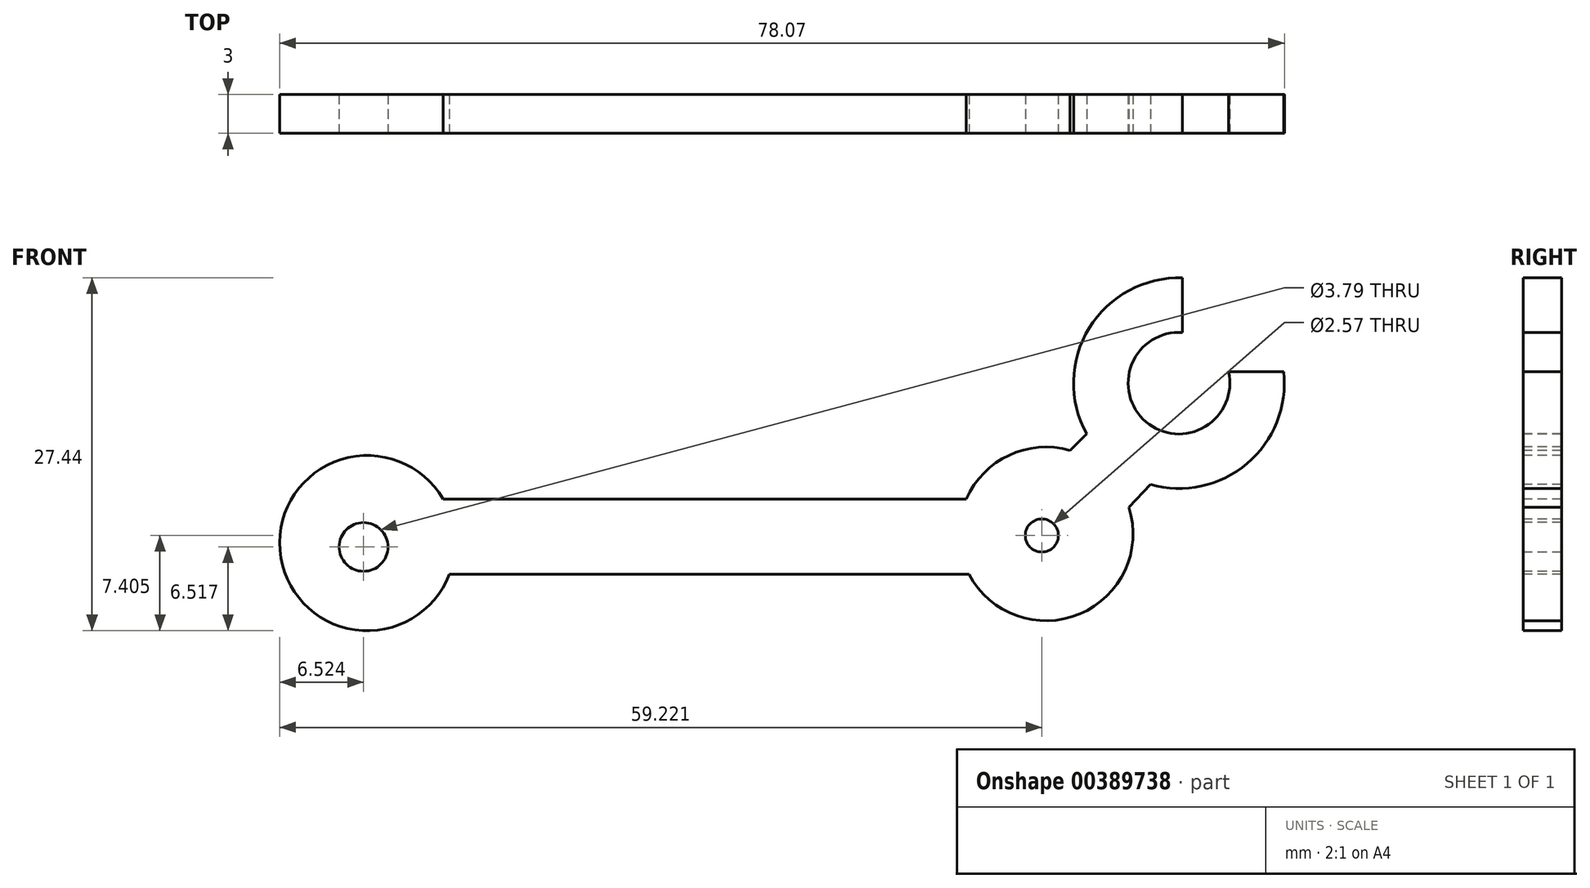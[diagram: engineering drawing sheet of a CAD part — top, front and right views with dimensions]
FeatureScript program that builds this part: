
annotation { "Feature Type Name" : "Feature", "Feature Type Description" : "" }
export const myFeature = defineFeature(function(context is Context, id is Id, definition is map)
    precondition{}
    {
        {
            var Q0;
            Q0=qCreatedBy(makeId("Front.planeOp"),FACE);
            var sketch = newSketch(context, id + "F0", { "sketchPlane" : qUnion([Q0])});
            skPoint(sketch, "E0.visualSharp", {"position": v(0, 0) * mm});
            skCircle(sketch, "E1", {"center": v(-5, 5.75) * mm, "radius": 6.76 * mm});
            skCircle(sketch, "E2", {"center": v(-57.73, 5.03) * mm, "radius": 6.82 * mm});
            skLineSegment(sketch, "E3", {"start": v(-51.84, 8.46) * mm, "end": v(-11.19, 8.46) * mm});
            skLineSegment(sketch, "E4", {"start": v(-51.36, 2.6) * mm, "end": v(-10.98, 2.6) * mm});
            skCircle(sketch, "E5", {"center": v(5.33, 17.47) * mm, "radius": 8.19 * mm});
            skLineSegment(sketch, "E6", {"start": v(1.43, 7.81) * mm, "end": v(3.1, 9.59) * mm});
            skLineSegment(sketch, "E7", {"start": v(-3.14, 12.24) * mm, "end": v(-1.85, 13.52) * mm});
            skLineSegment(sketch, "E8", {"start": v(9.18, 18.36) * mm, "end": v(13.47, 18.36) * mm});
            skCircle(sketch, "E9", {"center": v(5.33, 17.47) * mm, "radius": 3.95 * mm});
            skLineSegment(sketch, "E10", {"start": v(5.6, 21.4) * mm, "end": v(5.6, 25.65) * mm});
            skPoint(sketch, "E11", {"position": v(6.42, 21.26) * mm});
            skPoint(sketch, "E12", {"position": v(9.01, 18.9) * mm});
            skPoint(sketch, "E13", {"position": v(13.4, 18.9) * mm});
            skPoint(sketch, "E14", {"position": v(6.18, 25.61) * mm});
            skPoint(sketch, "E15", {"position": v(11.79, 22.5) * mm});
            skPoint(sketch, "E16", {"position": v(5.6, 21.4) * mm});
            skPoint(sketch, "E17", {"position": v(9.18, 18.36) * mm});
            skPoint(sketch, "E18", {"position": v(8.48, 19.85) * mm});
            skSolve(sketch);
        }
        {
            var Q0;
            {var subQ0=sQuery(id+"F0.wireOp",EDGE,"E2");var subQ1=makeQuery(id+"F0.imprint","INTERSECT",VERTEX,{"derivedFrom":[subQ0,sQuery(id+"F0.wireOp",EDGE,"E3")]});Q0=makeQuery(id+"F0.imprint","IMPRINT",FACE,{"disambiguationData":[TD([[makeQuery(id+"F0.imprint","IMPRINT",EDGE,{"disambiguationData":[TD([[subQ1,-1.0]])],"derivedFrom":subQ0}),1.0]])]});}
            var Q1;
            {var subQ0=sQuery(id+"F0.wireOp",EDGE,"E1");var subQ1=makeQuery(id+"F0.imprint","INTERSECT",VERTEX,{"derivedFrom":[subQ0,sQuery(id+"F0.wireOp",EDGE,"E6")]});Q1=makeQuery(id+"F0.imprint","IMPRINT",FACE,{"disambiguationData":[TD([[makeQuery(id+"F0.imprint","IMPRINT",EDGE,{"disambiguationData":[TD([[subQ1,-1.0]])],"derivedFrom":subQ0}),1.0]])]});}
            var Q2;
            {var subQ0=sQuery(id+"F0.wireOp",EDGE,"E3");Q2=makeQuery(id+"F0.imprint","IMPRINT",FACE,{"disambiguationData":[TD([[makeQuery(id+"F0.imprint","IMPRINT",EDGE,{"derivedFrom":subQ0}),-1.0]])]});}
            var Q3;
            {var subQ0=sQuery(id+"F0.wireOp",EDGE,"E6");Q3=makeQuery(id+"F0.imprint","IMPRINT",FACE,{"disambiguationData":[TD([[makeQuery(id+"F0.imprint","IMPRINT",EDGE,{"derivedFrom":subQ0}),1.0]])]});}
            var Q4;
            {var subQ2=sQuery(id+"F0.wireOp",EDGE,"E8");Q4=makeQuery(id+"F0.imprint","IMPRINT",FACE,{"disambiguationData":[TD([[makeQuery(id+"F0.imprint","IMPRINT",EDGE,{"derivedFrom":subQ2}),-1.0]])]});}
            extrude(context, id + "F1", {"entities" : qUnion([Q0, Q1, Q2, Q3, Q4]), "oppositeDirection" : true, "depth" : 3 * mm});
        }
        {
            var Q0;
            Q0=qCreatedBy(makeId("Front.planeOp"),FACE);
            var sketch = newSketch(context, id + "F2", { "sketchPlane" : qUnion([Q0])});
            skCircle(sketch, "E19", {"center": v(-5.33, 5.63) * mm, "radius": 1.28 * mm});
            skCircle(sketch, "E20", {"center": v(-58.03, 4.74) * mm, "radius": 1.9 * mm});
            skSolve(sketch);
        }
        {
            var Q0;
            Q0=makeQuery(id+"F2.imprint","IMPRINT",FACE,{"disambiguationData":[TD([[makeQuery(id+"F2.imprint","IMPRINT",EDGE,{"derivedFrom":sQuery(id+"F2.wireOp",EDGE,"E19")}),1.0]])]});
            var Q1;
            Q1=makeQuery(id+"F2.imprint","IMPRINT",FACE,{"disambiguationData":[TD([[makeQuery(id+"F2.imprint","IMPRINT",EDGE,{"derivedFrom":sQuery(id+"F2.wireOp",EDGE,"E20")}),1.0]])]});
            extrude(context, id + "F3", {"entities" : qUnion([Q0, Q1]), "operationType" : NewBodyOperationType.REMOVE, "oppositeDirection" : true, "depth" : 25 * mm});
        }
    });
